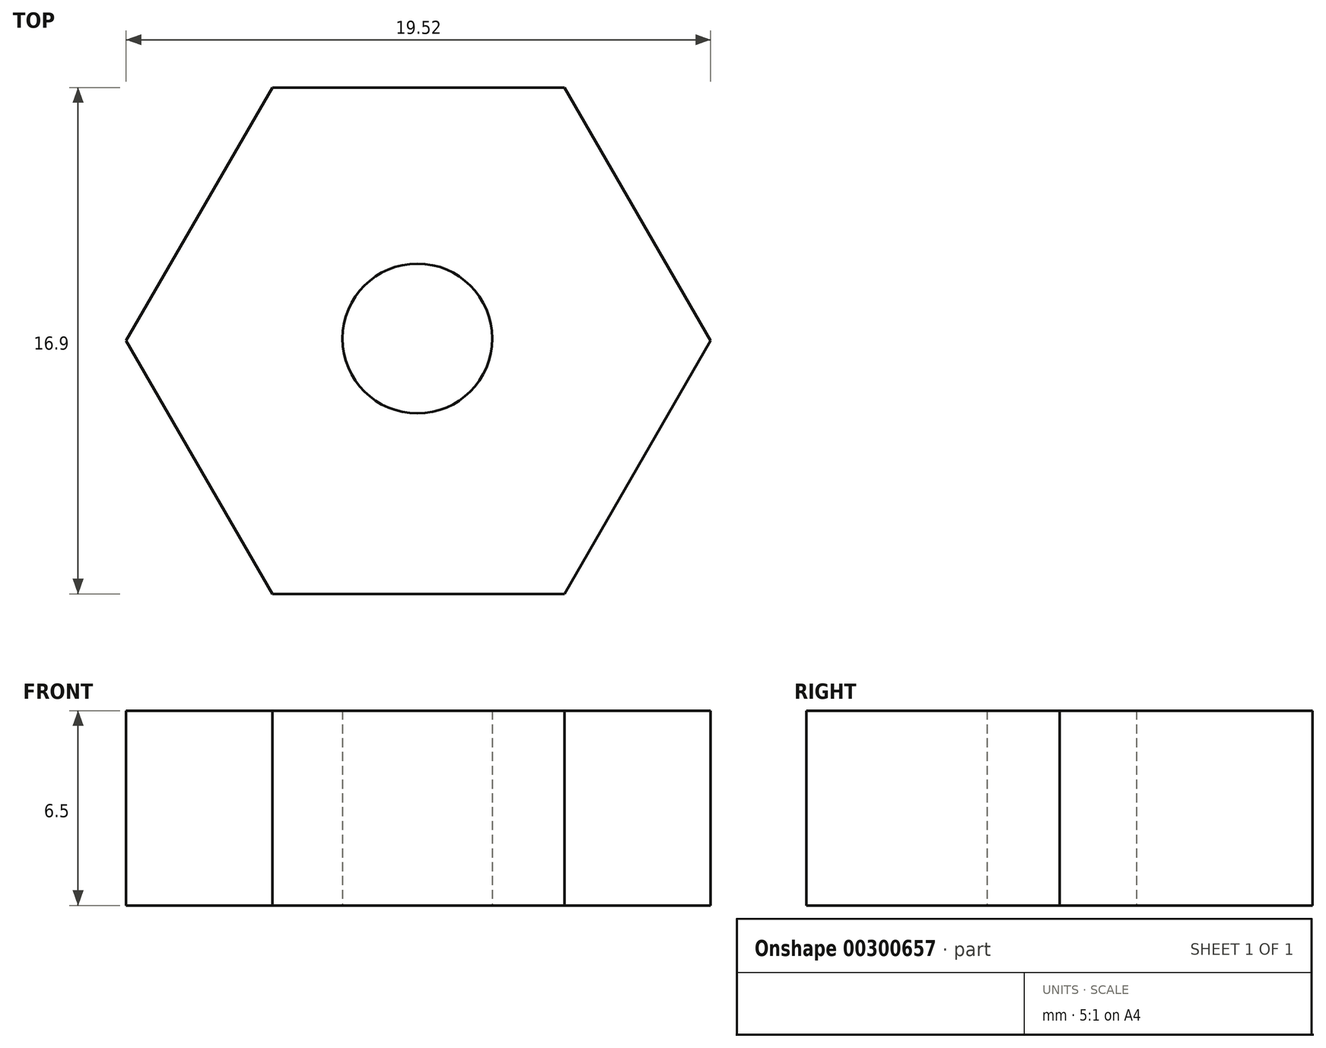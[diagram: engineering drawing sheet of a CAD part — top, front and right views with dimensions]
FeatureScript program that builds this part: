
annotation { "Feature Type Name" : "Feature", "Feature Type Description" : "" }
export const myFeature = defineFeature(function(context is Context, id is Id, definition is map)
    precondition{}
    {
        {
            var Q0;
            Q0=qCreatedBy(makeId("Top.planeOp"),FACE);
            var sketch = newSketch(context, id + "F0", { "sketchPlane" : qUnion([Q0])});
            skCircle(sketch, "E0.cCircle", {"center": v(0, 0) * mm, "radius": 8.45 * mm, "construction": true});
            skLineSegment(sketch, "E0.0", {"start": v(9.76, 0) * mm, "end": v(4.88, -8.45) * mm});
            skLineSegment(sketch, "E0.1", {"start": v(4.88, -8.45) * mm, "end": v(-4.88, -8.45) * mm});
            skLineSegment(sketch, "E0.2", {"start": v(-4.88, -8.45) * mm, "end": v(-9.76, 0) * mm});
            skLineSegment(sketch, "E0.3", {"start": v(-9.76, 0) * mm, "end": v(-4.88, 8.45) * mm});
            skLineSegment(sketch, "E0.4", {"start": v(-4.88, 8.45) * mm, "end": v(4.88, 8.45) * mm});
            skLineSegment(sketch, "E0.5", {"start": v(4.88, 8.45) * mm, "end": v(9.76, 0) * mm});
            skPoint(sketch, "E0.0.midPoint", {"position": v(7.32, -4.23) * mm});
            skCircle(sketch, "E1", {"center": v(-0.03, 0.07) * mm, "radius": 2.5 * mm});
            skSolve(sketch);
        }
        {
            var Q0;
            Q0=makeQuery(id+"F0.imprint","IMPRINT",FACE,{"disambiguationData":[TD([[makeQuery(id+"F0.imprint","IMPRINT",EDGE,{"derivedFrom":sQuery(id+"F0.wireOp",EDGE,"E0.0")}),-1.0]])]});
            extrude(context, id + "F1", {"entities" : qUnion([Q0]), "depth" : 6.5 * mm});
        }
    });
